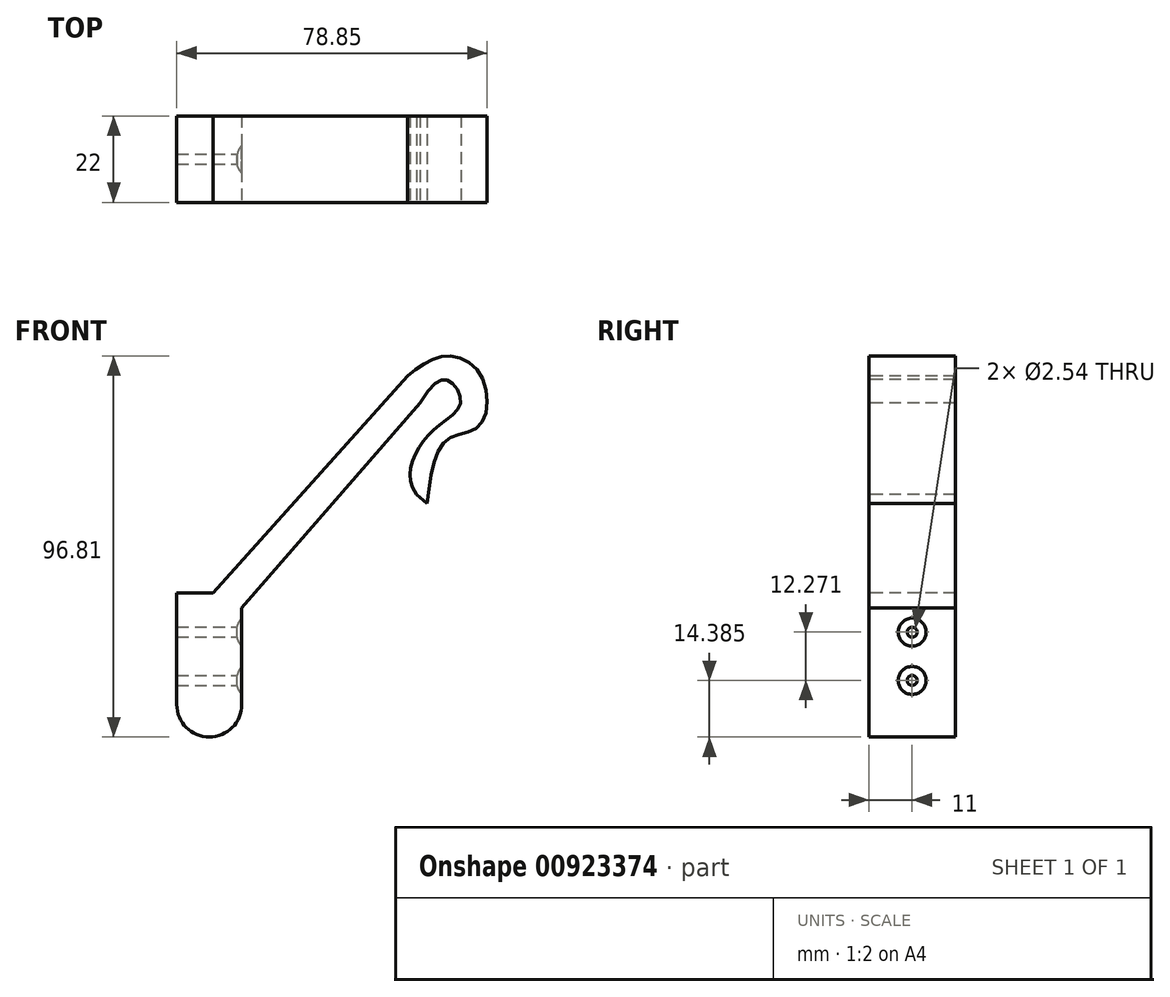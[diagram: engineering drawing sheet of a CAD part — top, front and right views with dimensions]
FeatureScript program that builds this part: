
annotation { "Feature Type Name" : "Feature", "Feature Type Description" : "" }
export const myFeature = defineFeature(function(context is Context, id is Id, definition is map)
    precondition{}
    {
        {
            var Q0;
            Q0=qCreatedBy(makeId("Front.planeOp"),FACE);
            var sketch = newSketch(context, id + "F0", { "sketchPlane" : qUnion([Q0])});
            skLineSegment(sketch, "E0", {"start": v(0, 0) * mm, "end": v(80, 0) * mm});
            skLineSegment(sketch, "E1", {"start": v(0, 0) * mm, "end": v(0, 100) * mm});
            skLineSegment(sketch, "E2", {"start": v(0, 100) * mm, "end": v(80, 100) * mm});
            skLineSegment(sketch, "E3", {"start": v(80, 100) * mm, "end": v(80, 0) * mm});
            skSolve(sketch);
        }
        {
            var Q0;
            Q0=makeQuery(id+"F0.imprint","IMPRINT",FACE,{"disambiguationData":[TD([[makeQuery(id+"F0.imprint","IMPRINT",EDGE,{"derivedFrom":sQuery(id+"F0.wireOp",EDGE,"E0")}),1.0]])]});
            extrude(context, id + "F1", {"entities" : qUnion([Q0]), "depth" : 22 * mm, "offsetDistance" : 25.4 * mm});
        }
        {
            var Q0;
            Q0=makeQuery(id+"F1.opExtrude","CAP_FACE",FACE,{"disambiguationData":[OSD([sQuery(id+"F0.wireOp",EDGE,"E0"),sQuery(id+"F0.wireOp",EDGE,"E1"),sQuery(id+"F0.wireOp",EDGE,"E2"),sQuery(id+"F0.wireOp",EDGE,"E3")])],"isStart":false});
            var sketch = newSketch(context, id + "F2", { "sketchPlane" : qUnion([Q0])});
            skLineSegment(sketch, "E4", {"start": v(0, 0) * mm, "end": v(0, 36.83) * mm});
            skLineSegment(sketch, "E5", {"start": v(0, 36.83) * mm, "end": v(9.25, 36.83) * mm});
            skLineSegment(sketch, "E6", {"start": v(9.25, 36.83) * mm, "end": v(58.58, 91.97) * mm});
            skLineSegment(sketch, "E7", {"start": v(0, 0) * mm, "end": v(16.5, 0) * mm});
            skLineSegment(sketch, "E8", {"start": v(16.5, 0) * mm, "end": v(16.5, 33.03) * mm});
            skLineSegment(sketch, "E9", {"start": v(16.5, 33.03) * mm, "end": v(61.82, 85.15) * mm});
            skFitSpline(sketch, "E10", {"points": [v(58.58, 91.97) * mm, v(68.13, 97.02) * mm, v(77.37, 91.97) * mm, v(76.86, 79.32) * mm, v(68.65, 75.73) * mm, v(63.52, 59.57) * mm], "startDerivative": vector(47.69, 37.36) * mm, "endDerivative": vector(-11.27, -85.32) * mm});
            skLineSegment(sketch, "E11", {"start": v(63.52, 59.57) * mm, "end": v(60.93, 61.82) * mm});
            skFitSpline(sketch, "E12", {"points": [v(61.82, 85.15) * mm, v(69.11, 90.71) * mm, v(72.12, 85.15) * mm, v(67.18, 79.85) * mm, v(61.82, 74.27) * mm, v(59.3, 67.93) * mm, v(60.93, 61.82) * mm], "startDerivative": vector(50.21, 81.66) * mm, "endDerivative": vector(28.63, -41.92) * mm});
            skSolve(sketch);
        }
        {
            var Q0;
            {var subQ2=sQuery(id+"F2.wireOp",EDGE,"E5");Q0=makeQuery(id+"F2.imprint","IMPRINT",FACE,{"disambiguationData":[TD([[makeQuery(id+"F2.imprint","IMPRINT",EDGE,{"derivedFrom":subQ2}),1.0]])]});}
            extrude(context, id + "F3", {"entities" : qUnion([Q0]), "operationType" : NewBodyOperationType.REMOVE, "oppositeDirection" : true, "depth" : 25.4 * mm, "offsetDistance" : 25.4 * mm});
        }
        {
            var Q0;
            Q0=makeQuery(id+"F1.opExtrude","CAP_FACE",FACE,{"disambiguationData":[OSD([sQuery(id+"F0.wireOp",EDGE,"E0"),sQuery(id+"F0.wireOp",EDGE,"E1"),sQuery(id+"F0.wireOp",EDGE,"E2"),sQuery(id+"F0.wireOp",EDGE,"E3")])],"isStart":false});
            var sketch = newSketch(context, id + "F4", { "sketchPlane" : qUnion([Q0])});
            skCircle(sketch, "E13", {"center": v(8.25, 8.49) * mm, "radius": 8.25 * mm});
            skPoint(sketch, "E13.centerSnap0", {"position": v(8.25, 0) * mm});
            skLineSegment(sketch, "E14", {"start": v(8.25, 8.49) * mm, "end": v(16.5, 8.49) * mm});
            skLineSegment(sketch, "E15", {"start": v(16.5, 8.49) * mm, "end": v(0, 8.49) * mm});
            skSolve(sketch);
        }
        {
            var Q0;
            {var subQ1=makeQuery(id+"F1.opExtrude","CAP_EDGE",EDGE,{"disambiguationData":[OSD([sQuery(id+"F0.wireOp",EDGE,"E1")])],"isStart":false});var subQ3=makeQuery(id+"F1.opExtrude","CAP_EDGE",EDGE,{"disambiguationData":[OSD([sQuery(id+"F0.wireOp",EDGE,"E0")])],"isStart":false});var subQ5=makeQuery(id+"F4.imprint","INTERSECT",VERTEX,{"derivedFrom":[subQ3,subQ1]});Q0=makeQuery(id+"F4.imprint","IMPRINT",FACE,{"disambiguationData":[TD([[makeQuery(id+"F4.imprint","IMPRINT",EDGE,{"disambiguationData":[TD([[subQ5,-1.0]])],"derivedFrom":subQ3}),1.0]])]});}
            var Q1;
            {var subQ1=makeQuery(id+"F3.boolean.opBoolean","COPY",EDGE,{"derivedFrom":makeQuery(id+"F3.opExtrude","CAP_EDGE",EDGE,{"disambiguationData":[OSD([sQuery(id+"F2.wireOp",EDGE,"E8")])],"isStart":true})});var subQ3=makeQuery(id+"F1.opExtrude","CAP_EDGE",EDGE,{"disambiguationData":[OSD([sQuery(id+"F0.wireOp",EDGE,"E0")])],"isStart":false});var subQ5=makeQuery(id+"F4.imprint","INTERSECT",VERTEX,{"derivedFrom":[subQ1,subQ3]});Q1=makeQuery(id+"F4.imprint","IMPRINT",FACE,{"disambiguationData":[TD([[makeQuery(id+"F4.imprint","IMPRINT",EDGE,{"disambiguationData":[TD([[subQ5,1.0]])],"derivedFrom":subQ3}),1.0]])]});}
            extrude(context, id + "F5", {"entities" : qUnion([Q0, Q1]), "operationType" : NewBodyOperationType.REMOVE, "oppositeDirection" : true, "depth" : 25.4 * mm, "offsetDistance" : 25.4 * mm});
        }
        {
            var Q0;
            Q0=makeQuery(id+"F3.boolean.opBoolean","COPY",FACE,{"derivedFrom":makeQuery(id+"F3.opExtrude","SWEPT_FACE",FACE,{"disambiguationData":[OSD([sQuery(id+"F2.wireOp",EDGE,"E8")])]})});
            var sketch = newSketch(context, id + "F6", { "sketchPlane" : qUnion([Q0])});
            skLineSegment(sketch, "E16.bottom", {"start": v(-22, 33.03) * mm, "end": v(0, 33.03) * mm});
            skLineSegment(sketch, "E16.top", {"start": v(-22, 8.49) * mm, "end": v(0, 8.49) * mm});
            skLineSegment(sketch, "E16.left", {"start": v(-22, 33.03) * mm, "end": v(-22, 8.49) * mm});
            skLineSegment(sketch, "E16.right", {"start": v(0, 33.03) * mm, "end": v(0, 8.49) * mm});
            skLineSegment(sketch, "E17", {"start": v(-22, 33.03) * mm, "end": v(-11, 33.03) * mm});
            skLineSegment(sketch, "E18", {"start": v(-11, 8.49) * mm, "end": v(-11, 20.76) * mm});
            skCircle(sketch, "E19", {"center": v(-11, 14.63) * mm, "radius": 3.56 * mm});
            skLineSegment(sketch, "E20", {"start": v(-11, 20.76) * mm, "end": v(-11, 33.03) * mm});
            skCircle(sketch, "E21", {"center": v(-11, 26.9) * mm, "radius": 3.56 * mm});
            skSolve(sketch);
        }
        {
            var Q0;
            {var subQ0=sQuery(id+"F6.wireOp",EDGE,"E21");var subQ1=sQuery(id+"F6.wireOp",EDGE,"E20");var subQ2=makeQuery(id+"F6.imprint","INTERSECT",VERTEX,{"disambiguationData":[OD(0.0)],"derivedFrom":[subQ1,subQ0]});Q0=makeQuery(id+"F6.imprint","IMPRINT",FACE,{"disambiguationData":[TD([[makeQuery(id+"F6.imprint","IMPRINT",EDGE,{"disambiguationData":[TD([[subQ2,-1.0]])],"derivedFrom":subQ1}),1.0]])]});}
            var Q1;
            {var subQ0=sQuery(id+"F6.wireOp",EDGE,"E21");var subQ1=sQuery(id+"F6.wireOp",EDGE,"E20");var subQ2=makeQuery(id+"F6.imprint","INTERSECT",VERTEX,{"disambiguationData":[OD(0.0)],"derivedFrom":[subQ1,subQ0]});Q1=makeQuery(id+"F6.imprint","IMPRINT",FACE,{"disambiguationData":[TD([[makeQuery(id+"F6.imprint","IMPRINT",EDGE,{"disambiguationData":[TD([[subQ2,-1.0]])],"derivedFrom":subQ1}),-1.0]])]});}
            var Q2;
            {var subQ0=sQuery(id+"F6.wireOp",EDGE,"E19");var subQ1=sQuery(id+"F6.wireOp",EDGE,"E18");var subQ2=makeQuery(id+"F6.imprint","INTERSECT",VERTEX,{"disambiguationData":[OD(0.0)],"derivedFrom":[subQ1,subQ0]});Q2=makeQuery(id+"F6.imprint","IMPRINT",FACE,{"disambiguationData":[TD([[makeQuery(id+"F6.imprint","IMPRINT",EDGE,{"disambiguationData":[TD([[subQ2,-1.0]])],"derivedFrom":subQ1}),1.0]])]});}
            var Q3;
            {var subQ0=sQuery(id+"F6.wireOp",EDGE,"E19");var subQ1=sQuery(id+"F6.wireOp",EDGE,"E18");var subQ2=makeQuery(id+"F6.imprint","INTERSECT",VERTEX,{"disambiguationData":[OD(0.0)],"derivedFrom":[subQ1,subQ0]});Q3=makeQuery(id+"F6.imprint","IMPRINT",FACE,{"disambiguationData":[TD([[makeQuery(id+"F6.imprint","IMPRINT",EDGE,{"disambiguationData":[TD([[subQ2,-1.0]])],"derivedFrom":subQ1}),-1.0]])]});}
            extrude(context, id + "F7", {"entities" : qUnion([Q0, Q1, Q2, Q3]), "operationType" : NewBodyOperationType.REMOVE, "oppositeDirection" : true, "depth" : 1.27 * mm, "offsetDistance" : 25.4 * mm});
        }
        {
            var Q0;
            Q0=makeQuery(id+"F7.boolean.opBoolean","COPY",EDGE,{"derivedFrom":makeQuery(id+"F7.opExtrude","CAP_EDGE",EDGE,{"disambiguationData":[OSD([sQuery(id+"F6.wireOp",EDGE,"E21")])],"isStart":false})});
            var Q1;
            Q1=makeQuery(id+"F7.boolean.opBoolean","COPY",FACE,{"derivedFrom":makeQuery(id+"F7.opExtrude","CAP_FACE",FACE,{"disambiguationData":[OSD([sQuery(id+"F6.wireOp",EDGE,"E19")])],"isStart":false})});
            fillet(context, id + "F8", {"entities" : qUnion([Q0, Q1]), "radius" : 5.08 * mm, "tangentPropagation" : true, "allowEdgeOverflow" : false});
        }
        {
            var Q0;
            Q0=makeQuery(id+"F7.boolean.opBoolean","COPY",FACE,{"derivedFrom":makeQuery(id+"F7.opExtrude","CAP_FACE",FACE,{"disambiguationData":[OSD([sQuery(id+"F6.wireOp",EDGE,"E21")])],"isStart":false})});
            var sketch = newSketch(context, id + "F9", { "sketchPlane" : qUnion([Q0])});
            skCircle(sketch, "E22", {"center": v(-11, 26.9) * mm, "radius": 1.27 * mm});
            skSolve(sketch);
        }
        {
            var Q0;
            Q0 = qSketchRegion(id + "F9", true);
            extrude(context, id + "F10", {"entities" : qUnion([Q0]), "operationType" : NewBodyOperationType.REMOVE, "endBound" : BoundingType.THROUGH_ALL, "oppositeDirection" : true, "depth" : 25.4 * mm, "offsetDistance" : 25.4 * mm});
        }
        {
            var Q0;
            Q0=makeQuery(id+"F1.opExtrude","SWEPT_FACE",FACE,{"disambiguationData":[OSD([sQuery(id+"F0.wireOp",EDGE,"E1")])]});
            var sketch = newSketch(context, id + "F11", { "sketchPlane" : qUnion([Q0])});
            skCircle(sketch, "E23", {"center": v(11, 26.9) * mm, "radius": 1.27 * mm});
            skSolve(sketch);
        }
        {
            var Q0;
            Q0 = qSketchRegion(id + "F11", true);
            extrude(context, id + "F12", {"entities" : qUnion([Q0]), "operationType" : NewBodyOperationType.REMOVE, "oppositeDirection" : true, "depth" : 25.4 * mm, "offsetDistance" : 25.4 * mm});
        }
        {
            var Q0;
            Q0=makeQuery(id+"F7.boolean.opBoolean","COPY",FACE,{"derivedFrom":makeQuery(id+"F7.opExtrude","CAP_FACE",FACE,{"disambiguationData":[OSD([sQuery(id+"F6.wireOp",EDGE,"E19")])],"isStart":false})});
            var sketch = newSketch(context, id + "F13", { "sketchPlane" : qUnion([Q0])});
            skCircle(sketch, "E24", {"center": v(-11, 14.63) * mm, "radius": 1.27 * mm});
            skSolve(sketch);
        }
        {
            var Q0;
            Q0 = qSketchRegion(id + "F13", true);
            extrude(context, id + "F14", {"entities" : qUnion([Q0]), "operationType" : NewBodyOperationType.REMOVE, "oppositeDirection" : true, "depth" : 25.4 * mm, "offsetDistance" : 25.4 * mm});
        }
        {
            var Q0;
            Q0=makeQuery(id+"F14.boolean.opBoolean","COPY",FACE,{"derivedFrom":makeQuery(id+"F14.opExtrude","CAP_FACE",FACE,{"disambiguationData":[OSD([sQuery(id+"F13.wireOp",EDGE,"E24")])],"isStart":true})});
            var sketch = newSketch(context, id + "F15", { "sketchPlane" : qUnion([Q0])});
            skCircle(sketch, "E25", {"center": v(11, 14.63) * mm, "radius": 1.27 * mm});
            skSolve(sketch);
        }
        {
            var Q0;
            Q0 = qSketchRegion(id + "F15", true);
            extrude(context, id + "F16", {"entities" : qUnion([Q0]), "operationType" : NewBodyOperationType.REMOVE, "oppositeDirection" : true, "depth" : 25.4 * mm, "offsetDistance" : 25.4 * mm});
        }
    });
